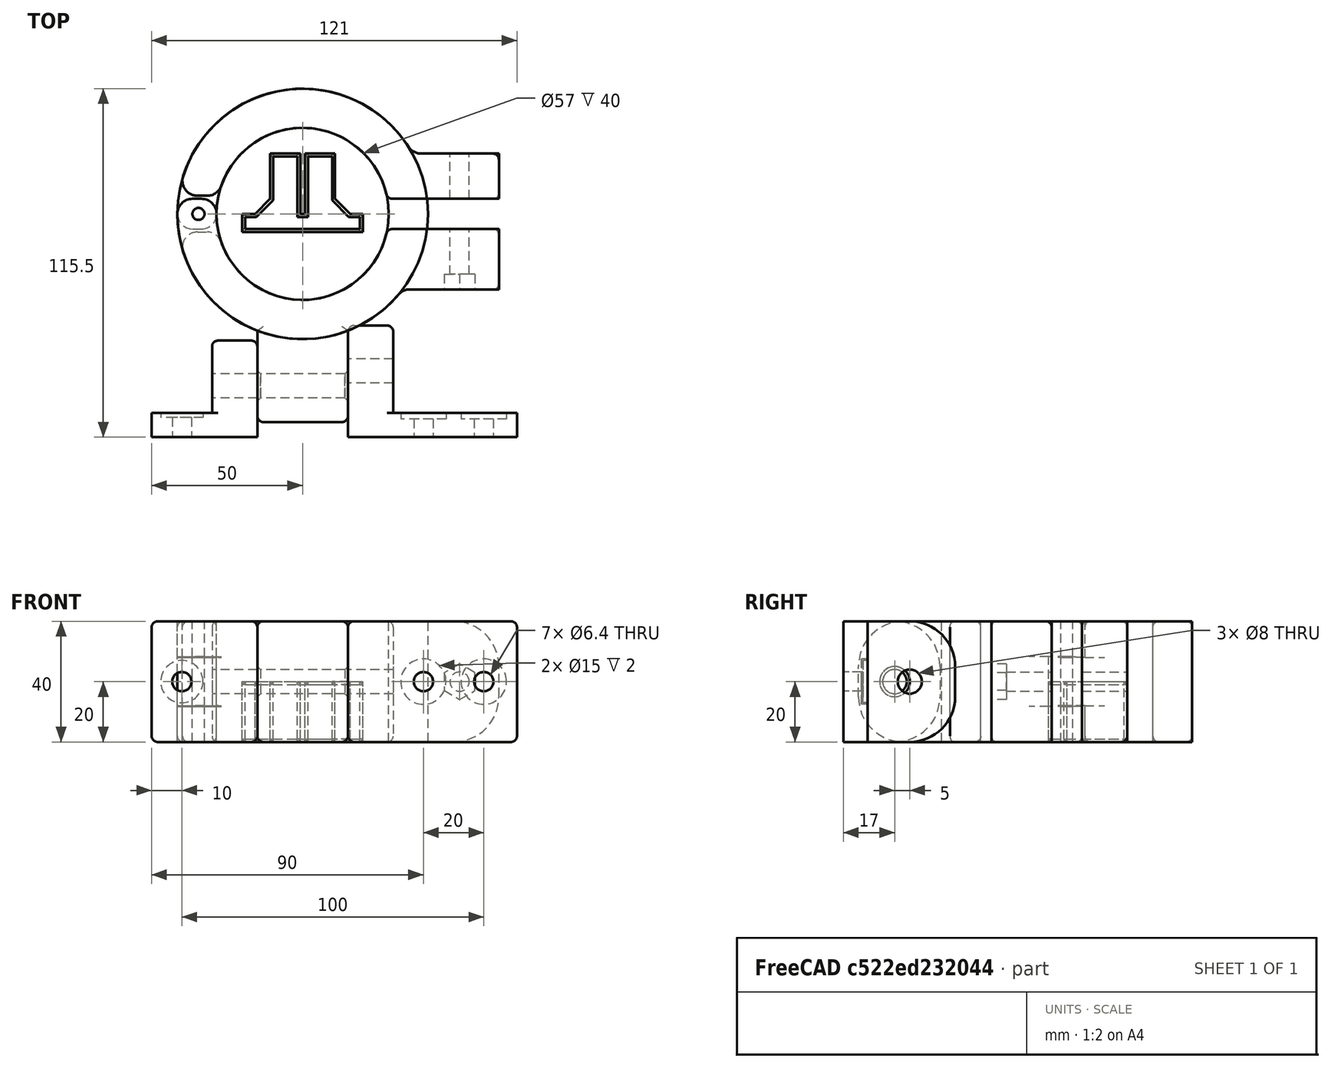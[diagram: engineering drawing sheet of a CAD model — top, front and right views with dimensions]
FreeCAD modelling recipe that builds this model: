
FCSTD DOCUMENT  (FreeCAD 0.18R16146 (Git))
Label: grinder-mounter
License: All rights reserved
LicenseURL: http://en.wikipedia.org/wiki/All_rights_reserved
objects: Part::Fillet×19, Part::Cut×18, Part::Box×17, Part::Cylinder×15, Part::MultiFuse×8, Part::Feature×6, Part::Chamfer×3
note: 86 computed .brp shape members not serialized (recipe doc carries the construction recipe); baked Part::Feature solids carry a one-line shape summary decoded from their .brp

FEATURE [Part::Cylinder] Cylinder
  Angle = 360
  AttacherType = Attacher::AttachEngine3D
  Height = 40
  Radius = 28.5
FEATURE [Part::Cylinder] Cylinder001
  Angle = 360
  AttacherType = Attacher::AttachEngine3D
  Height = 40
  Radius = 41.5
FEATURE [Part::Cut] Cut  label="ring"
  Base = -> Cylinder001
  Tool = -> Cylinder
FEATURE [Part::Feature] Cut001  label="ring001"
  shape: bbox 83 x 83 x 40 mm, 4 faces (baked)
FEATURE [Part::Feature] Cut002  label="ring002"
  shape: bbox 83 x 83 x 40 mm, 4 faces (baked)
FEATURE [Part::Box] Box  label="Cube"
  AttacherType = Attacher::AttachEngine3D
  Height = 41
  Length = 92
  Placement = pos=(-50,5,0) rot=(0,0,1;0rad)
  Width = 48
FEATURE [Part::Box] Box001  label="Cube001"
  AttacherType = Attacher::AttachEngine3D
  Height = 41
  Length = 21
  Placement = pos=(25,-5,0) rot=(0,0,1;0rad)
  Width = 10
FEATURE [Part::Cut] Cut003
  Base = -> Cut002
  Tool = -> Box
FEATURE [Part::Cut] Cut004
  Base = -> Cut003
  Tool = -> Box001
FEATURE [Part::Box] Box002  label="Cube002"
  AttacherType = Attacher::AttachEngine3D
  Height = 41
  Length = 22
  Placement = pos=(25,-5,0) rot=(0,0,1;0rad)
  Width = 10
FEATURE [Part::Box] Box003  label="Cube003"
  AttacherType = Attacher::AttachEngine3D
  Height = 41
  Length = 88
  Placement = pos=(-45,-50,0) rot=(0,0,1;0rad)
  Width = 45
FEATURE [Part::Cut] Cut005
  Base = -> Cut001
  Tool = -> Box003
FEATURE [Part::Cut] Cut006
  Base = -> Cut005
  Tool = -> Box002
FEATURE [Part::Cylinder] Cylinder002
  Angle = 360
  AttacherType = Attacher::AttachEngine3D
  Height = 50
  Placement = pos=(-34.5,0,0) rot=(0,0,1;0rad)
  Radius = 2
FEATURE [Part::Cylinder] Cylinder003
  Angle = 360
  AttacherType = Attacher::AttachEngine3D
  Height = 50
  Placement = pos=(-34.5,0,0) rot=(0,0,1;0rad)
  Radius = 2
FEATURE [Part::Cut] Cut007
  Base = -> Cut006
  Tool = -> Cylinder002
FEATURE [Part::Cut] Cut008
  Base = -> Cut004
  Tool = -> Cylinder003
FEATURE [Part::Box] Box004  label="Cube004"
  AttacherType = Attacher::AttachEngine3D
  Height = 12
  Length = 26
  Placement = pos=(-48,-6,0) rot=(0,0,1;0rad)
  Width = 12
FEATURE [Part::Box] Box005  label="Cube005"
  AttacherType = Attacher::AttachEngine3D
  Height = 12
  Length = 26
  Placement = pos=(-48,-6,28) rot=(0,0,1;0rad)
  Width = 12
FEATURE [Part::Cut] Cut009
  Base = -> Cut007
  Tool = -> Box005
FEATURE [Part::Cut] Cut010
  Base = -> Cut009
  Tool = -> Box004
FEATURE [Part::Box] Box006  label="Cube006"
  AttacherType = Attacher::AttachEngine3D
  Height = 16.5
  Length = 26
  Placement = pos=(-48,-6,11.75) rot=(0,0,1;0rad)
  Width = 12
FEATURE [Part::Cut] Cut011
  Base = -> Cut008
  Tool = -> Box006
FEATURE [Part::Fillet] Fillet
  Base = -> Cut010
  Edges = 4 edges r=5: [Edge2,Edge6,Edge13,Edge23]
FEATURE [Part::Fillet] Fillet001
  Base = -> Fillet
  Edges = 2 edges r=5: [Edge8,Edge33]
FEATURE [Part::Fillet] Fillet002
  Base = -> Cut011
  Edges = 6 edges r=5: [Edge2,Edge4,Edge6,Edge13,Edge18,Edge23]
FEATURE [Part::Box] Box007  label="Cube007"
  AttacherType = Attacher::AttachEngine3D
  Height = 40
  Length = 30
  Placement = pos=(-15,-69,0) rot=(0,0,1;0rad)
  Width = 38
FEATURE [Part::Box] Box008  label="Cube008"
  AttacherType = Attacher::AttachEngine3D
  Height = 40
  Length = 35
  Placement = pos=(30,5,0) rot=(0,0,1;0rad)
  Width = 15
FEATURE [Part::Box] Box009  label="Cube009"
  AttacherType = Attacher::AttachEngine3D
  Height = 40
  Length = 35
  Placement = pos=(30,-25,0) rot=(0,0,1;0rad)
  Width = 20
FEATURE [Part::Cylinder] Cylinder004
  Angle = 360
  AttacherType = Attacher::AttachEngine3D
  Height = 42
  Placement = pos=(20,-57,20) rot=(0,-1,0;1.5708rad)
  Radius = 4
FEATURE [Part::Cut] Cut012
  Base = -> Box007
  Tool = -> Cylinder004
FEATURE [Part::Fillet] Fillet003
  Base = -> Cut012
  Edges = 2 edges r=15: [Edge6,Edge8]
FEATURE [Part::Cylinder] Cylinder005
  Angle = 360
  AttacherType = Attacher::AttachEngine3D
  Height = 81
  Placement = pos=(43,-52,20) rot=(0,-1,0;1.5708rad)
  Radius = 4
FEATURE [Part::Box] Box010  label="Cube010"
  AttacherType = Attacher::AttachEngine3D
  Height = 40
  Length = 15
  Placement = pos=(15,-74,0) rot=(0,0,1;0rad)
  Width = 37
FEATURE [Part::Box] Box011  label="Cube011"
  AttacherType = Attacher::AttachEngine3D
  Height = 40
  Length = 15
  Placement = pos=(-30,-74,0) rot=(0,0,1;0rad)
  Width = 32
FEATURE [Part::Box] Box012  label="Cube012"
  AttacherType = Attacher::AttachEngine3D
  Height = 40
  Length = 56
  Placement = pos=(15,-74,0) rot=(0,0,1;0rad)
  Width = 8
FEATURE [Part::Box] Box013  label="Cube013"
  AttacherType = Attacher::AttachEngine3D
  Height = 40
  Length = 35
  Placement = pos=(-50,-74,0) rot=(0,0,1;0rad)
  Width = 8
FEATURE [Part::Fillet] Fillet005
  Base = -> Box011
  Edges = 2 edges r=15: [Edge11,Edge12]
FEATURE [Part::Cylinder] Cylinder006
  Angle = 360
  AttacherType = Attacher::AttachEngine3D
  Height = 81
  Placement = pos=(43,-57,20) rot=(0,-1,0;1.5708rad)
  Radius = 4
FEATURE [Part::Cut] Cut014
  Base = -> Fillet005
  Tool = -> Cylinder006
FEATURE [Part::Cylinder] Cylinder007
  Angle = 360
  AttacherType = Attacher::AttachEngine3D
  Height = 71
  Placement = pos=(52,-35,20) rot=(-1,0,0;1.5708rad)
  Radius = 3.2
FEATURE [Part::Fillet] Fillet006
  Base = -> Fillet001
  Edges = 1 edges r=2: [Edge39]
FEATURE [Part::Fillet] Fillet007
  Base = -> Fillet002
  Edges = 1 edges r=2: [Edge20]
FEATURE [Part::Feature] Body001
  Placement = pos=(52,-20,20) rot=(1,0,0;1.5708rad)
  shape: bbox 10.22 x 5 x 11.8 mm, 8 faces (baked)
FEATURE [Part::MultiFuse] Fusion001
  Shapes = -> [Box009,Fillet007]
FEATURE [Part::Fillet] Fillet009
  Base = -> Fusion001
  Edges = 1 edges r=5: [Edge29]
FEATURE [Part::MultiFuse] Fusion
  Shapes = -> [Box008,Fillet006]
FEATURE [Part::Fillet] Fillet010
  Base = -> Fusion
  Edges = 1 edges r=5: [Edge51]
FEATURE [Part::Cut] Cut015
  Base = -> Fillet009
  Tool = -> Body001
FEATURE [Part::Cylinder] Cylinder008
  Angle = 360
  AttacherType = Attacher::AttachEngine3D
  Height = 71
  Placement = pos=(52,-35,20) rot=(-1,0,0;1.5708rad)
  Radius = 3.2
FEATURE [Part::Cut] Cut016
  Base = -> Cut015
  Tool = -> Cylinder007
FEATURE [Part::Cut] Cut017
  Base = -> Fillet010
  Tool = -> Cylinder008
FEATURE [Part::Fillet] Fillet011
  Base = -> Cut016
  Edges = 2 edges r=15: [Edge3,Edge27]
FEATURE [Part::Fillet] Fillet012
  Base = -> Cut017
  Edges = 2 edges r=15: [Edge22,Edge69]
FEATURE [Part::Feature] Fillet011001  label="Fillet013"
  shape: bbox 106.5 x 46.5 x 40 mm, 32 faces (baked)
FEATURE [Part::Feature] Fillet012001  label="Fillet014"
  shape: bbox 106.5 x 46.5 x 40 mm, 24 faces (baked)
FEATURE [Part::Fillet] Fillet012002
  Base = -> Fillet011001
  Edges = 24 edges r=2: [Edge1,Edge2,Edge4,Edge5,Edge6,Edge15,Edge18,Edge19,Edge21,Edge22,Edge35,Edge37,Edge46,Edge49,Edge52,Edge53,Edge56,Edge62,Edge64,Edge74,Edge84,Edge87,Edge90,Edge91]
FEATURE [Part::Fillet] Fillet012003
  Base = -> Fillet012001
  Edges = 24 edges r=2: [Edge1,Edge2,Edge4,Edge5,Edge6,Edge8,Edge11,Edge13,Edge14,Edge16,Edge20,Edge22,Edge29,Edge32,Edge35,Edge38,Edge41,Edge47,Edge49,Edge56,Edge65,Edge67,Edge69,Edge70]
FEATURE [Part::Fillet] Fillet012004
  Base = -> Fillet003
  Edges = 10 edges r=2: [Edge1,Edge2,Edge3,Edge4,Edge5,Edge8,Edge12,Edge14,Edge16,Edge18]
FEATURE [Part::Chamfer] Chamfer
  Base = -> Fillet012004
  Edges = 2 edges r=1: [Edge7,Edge25]
FEATURE [Part::MultiFuse] Fusion002
  Shapes = -> [Fillet012002,Chamfer]
FEATURE [Part::Fillet] Fillet012005
  Base = -> Cut014
  Edges = 10 edges r=2: [Edge1,Edge2,Edge4,Edge5,Edge6,Edge10,Edge12,Edge15,Edge18,Edge19]
FEATURE [Part::Fillet] Fillet012007
  Base = -> Box013
  Edges = 4 edges r=2: [Edge2,Edge4,Edge6,Edge8]
FEATURE [Part::MultiFuse] Fusion004
  Shapes = -> [Fillet012007,Fillet012005]
FEATURE [Part::Cylinder] Cylinder009
  Angle = 360
  AttacherType = Attacher::AttachEngine3D
  Height = 10
  Placement = pos=(40,-64,20) rot=(1,0,0;1.5708rad)
  Radius = 3.2
FEATURE [Part::Cylinder] Cylinder010
  Angle = 360
  AttacherType = Attacher::AttachEngine3D
  Height = 10
  Placement = pos=(-40,-64,20) rot=(1,0,0;1.5708rad)
  Radius = 3.2
FEATURE [Part::Cylinder] Cylinder011
  Angle = 360
  AttacherType = Attacher::AttachEngine3D
  Height = 1.5
  Placement = pos=(-40,-66,20) rot=(1,0,0;1.5708rad)
  Radius = 7
FEATURE [Part::Cylinder] Cylinder012
  Angle = 360
  AttacherType = Attacher::AttachEngine3D
  Height = 2
  Placement = pos=(40,-66,20) rot=(1,0,0;1.5708rad)
  Radius = 7.5
FEATURE [Part::MultiFuse] Fusion006
  Shapes = -> [Cylinder011,Cylinder010]
FEATURE [Part::Cut] Cut019
  Base = -> Fusion004
  Tool = -> Fusion006
FEATURE [Part::Box] Box014  label="Cube014"
  AttacherType = Attacher::AttachEngine3D
  Height = 20
  Length = 10
  Placement = pos=(0.75,0,0) rot=(0,0,1;0rad)
  Width = 20
FEATURE [Part::Box] Box015  label="Cube015"
  AttacherType = Attacher::AttachEngine3D
  Height = 20
  Length = 10
  Placement = pos=(-10.75,0,0) rot=(0,0,1;0rad)
  Width = 20
FEATURE [Part::Box] Box016  label="Cube016"
  AttacherType = Attacher::AttachEngine3D
  Height = 20
  Length = 40
  Placement = pos=(-20,-6,0) rot=(0,0,1;0rad)
  Width = 6
FEATURE [Part::MultiFuse] Fusion007
  Shapes = -> [Box016,Box015,Box014]
FEATURE [Part::Chamfer] Chamfer001
  Base = -> Fusion007
  Edges = 2 edges r=5: [Edge15,Edge30]
FEATURE [Part::Feature] Chamfer001001  label="Chamfer002"
  shape: bbox 40 x 26 x 20 mm, 16 faces (baked)
FEATURE [Part::Chamfer] Chamfer001002  label="1p5mm-alinner"
  Base = -> Chamfer001001
  Edges = 36 edges r=1: [Edge1,Edge3,Edge5,Edge6,Edge7,Edge8,Edge10,Edge11,Edge12,Edge13,Edge14,Edge15,Edge16,Edge17,Edge18,Edge19,Edge20,Edge21,Edge23,Edge24,Edge26,Edge27,Edge28,Edge29,Edge30,Edge31,Edge32,Edge33,Edge34,Edge35,Edge37,Edge38,Edge39,Edge40,Edge41,Edge42]
FEATURE [Part::Cylinder] Cylinder013
  Angle = 360
  AttacherType = Attacher::AttachEngine3D
  Height = 2
  Placement = pos=(60,-66,20) rot=(1,0,0;1.5708rad)
  Radius = 7.5
FEATURE [Part::Cylinder] Cylinder014
  Angle = 360
  AttacherType = Attacher::AttachEngine3D
  Height = 10
  Placement = pos=(60,-64,20) rot=(1,0,0;1.5708rad)
  Radius = 3.2
FEATURE [Part::MultiFuse] Fusion008
  Shapes = -> [Cylinder012,Cylinder009,Cylinder014,Cylinder013]
FEATURE [Part::Cut] Cut020
  Base = -> Box012
  Tool = -> Fusion008
FEATURE [Part::Cut] Cut021
  Base = -> Box010
  Tool = -> Cylinder005
FEATURE [Part::Fillet] Fillet012008
  Base = -> Cut021
  Edges = 2 edges r=15: [Edge9,Edge11]
FEATURE [Part::Fillet] Fillet012009
  Base = -> Cut020
  Edges = 4 edges r=2: [Edge2,Edge4,Edge11,Edge16]
FEATURE [Part::Fillet] Fillet012010
  Base = -> Fillet012008
  Edges = 10 edges r=2: [Edge1,Edge2,Edge4,Edge5,Edge6,Edge10,Edge12,Edge15,Edge18,Edge19]
FEATURE [Part::MultiFuse] Fusion009
  Shapes = -> [Fillet012009,Fillet012010]
